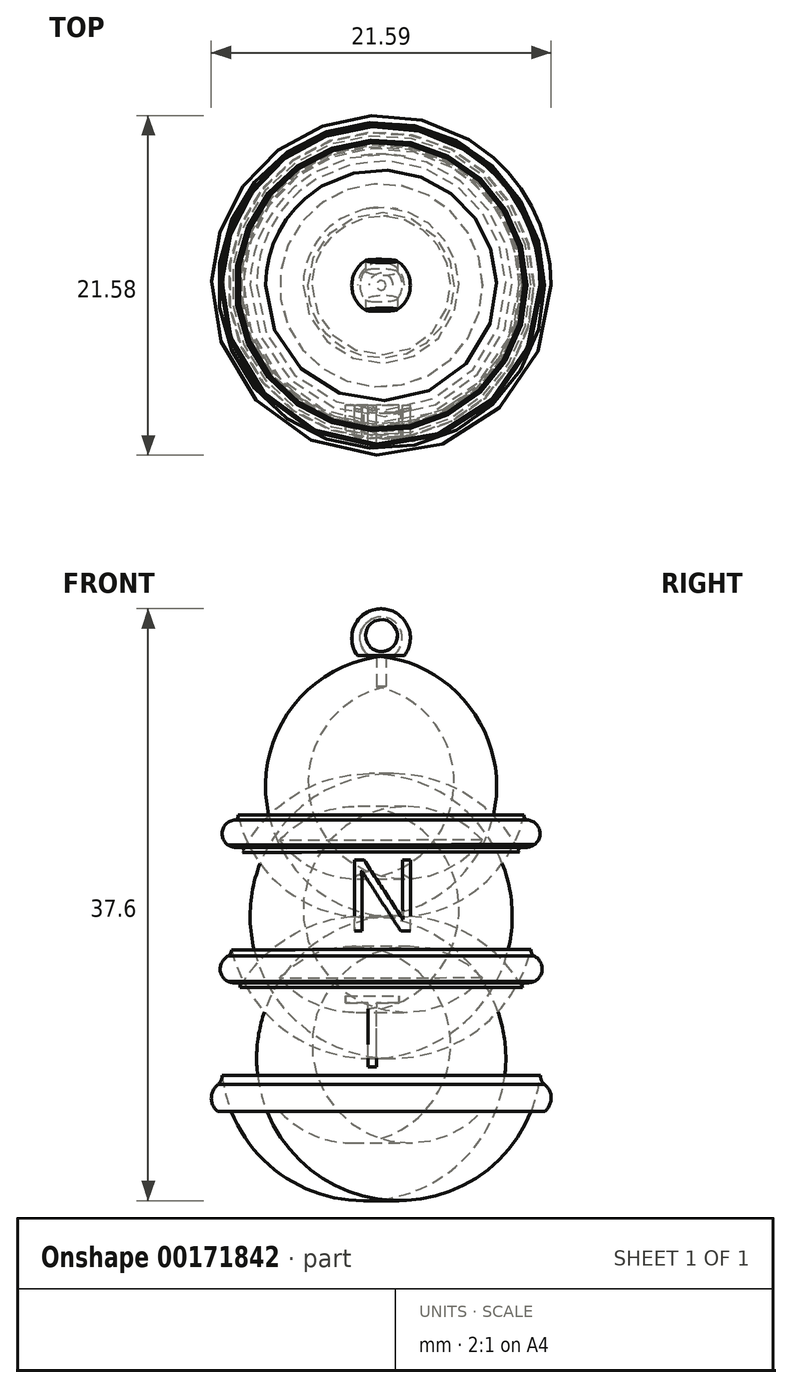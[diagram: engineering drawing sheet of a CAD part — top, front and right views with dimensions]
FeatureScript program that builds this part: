
annotation { "Feature Type Name" : "Feature", "Feature Type Description" : "" }
export const myFeature = defineFeature(function(context is Context, id is Id, definition is map)
    precondition{}
    {
        {
            var Q0;
            Q0=qCreatedBy(makeId("Front.planeOp"),FACE);
            var sketch = newSketch(context, id + "F0", { "sketchPlane" : qUnion([Q0])});
            skLineSegment(sketch, "E0.bottom", {"start": v(-21.86, 0.08) * mm, "end": v(-21.89, 0.08) * mm, "construction": true});
            skLineSegment(sketch, "E0.top", {"start": v(-9.19, 50.88) * mm, "end": v(-34.59, 50.88) * mm, "construction": true});
            skLineSegment(sketch, "E0.left", {"start": v(-9.19, 0.08) * mm, "end": v(-9.19, 50.88) * mm, "construction": true});
            skLineSegment(sketch, "E0.right", {"start": v(-34.59, 0.08) * mm, "end": v(-34.59, 50.88) * mm, "construction": true});
            skLineSegment(sketch, "E1.left", {"start": v(-34.48, 0.28) * mm, "end": v(-34.59, 0.08) * mm});
            skLineSegment(sketch, "E1.right", {"start": v(-44.55, 0.28) * mm, "end": v(-44.66, 0.08) * mm});
            skLineSegment(sketch, "E2", {"start": v(-31.55, 20.94) * mm, "end": v(-30.06, 20.94) * mm});
            skLineSegment(sketch, "E3", {"start": v(-21.86, -2.43) * mm, "end": v(-21.85, 22.57) * mm, "construction": true});
            skLineSegment(sketch, "E4", {"start": v(-31.55, 19.56) * mm, "end": v(-31.55, 14.27) * mm});
            skLineSegment(sketch, "E5", {"start": v(-31.44, 12.9) * mm, "end": v(-30.12, 12.9) * mm});
            skLineSegment(sketch, "E6", {"start": v(-29.62, 0.08) * mm, "end": v(-21.87, 0.08) * mm});
            skLineSegment(sketch, "E7", {"start": v(-30.06, 20.94) * mm, "end": v(-30.06, 14.45) * mm});
            skLineSegment(sketch, "E8", {"start": v(-30.06, 14.45) * mm, "end": v(-28.15, 14.45) * mm});
            skLineSegment(sketch, "E9", {"start": v(-30.12, 12.9) * mm, "end": v(-29.62, 0.08) * mm});
            skLineSegment(sketch, "E10", {"start": v(-28.15, 14.45) * mm, "end": v(-27.8, 1.73) * mm});
            skPoint(sketch, "E11.orphan", {"position": v(-26.25, 14.45) * mm});
            skLineSegment(sketch, "E12.trimOffspring", {"start": v(-29.62, 0.08) * mm, "end": v(-34.59, 0.08) * mm, "construction": true});
            skLineSegment(sketch, "E13", {"start": v(-27.8, 1.73) * mm, "end": v(-21.87, 1.73) * mm});
            skLineSegment(sketch, "E14", {"start": v(-21.87, 1.73) * mm, "end": v(-21.87, 0.08) * mm});
            skLineSegment(sketch, "E15.trimOffspring", {"start": v(-21.87, 0.08) * mm, "end": v(-29.62, 0.08) * mm, "construction": true});
            skArc(sketch, "E16", {"start": v(-31.55, 20.94) * mm, "mid": v(-32.24, 20.25) * mm, "end": v(-31.55, 19.56) * mm});
            skArc(sketch, "E17", {"start": v(-31.55, 14.27) * mm, "mid": v(-32.12, 13.53) * mm, "end": v(-31.44, 12.9) * mm});
            skSolve(sketch);
        }
        {
            var Q0;
            Q0=sQuery(id+"F0.wireOp",EDGE,"E2");
            var Q1;
            Q1=sQuery(id+"F0.wireOp",EDGE,"E7");
            var Q2;
            Q2=sQuery(id+"F0.wireOp",EDGE,"E16");
            var Q3;
            Q3=sQuery(id+"F0.wireOp",EDGE,"E4");
            var Q4;
            Q4=sQuery(id+"F0.wireOp",EDGE,"E17");
            var Q5;
            Q5=sQuery(id+"F0.wireOp",EDGE,"E5");
            var Q6;
            Q6=sQuery(id+"F0.wireOp",EDGE,"E8");
            var Q7;
            Q7=sQuery(id+"F0.wireOp",EDGE,"E10");
            var Q8;
            Q8=sQuery(id+"F0.wireOp",EDGE,"E9");
            var Q9;
            Q9=sQuery(id+"F0.wireOp",EDGE,"E6");
            var Q10;
            Q10=sQuery(id+"F0.wireOp",EDGE,"E13");
            var Q11;
            Q11=sQuery(id+"F0.wireOp",EDGE,"E3");
            revolve(context, id + "F1", {"bodyType" : ToolBodyType.SURFACE, "surfaceEntities" : qUnion([Q0, Q1, Q2, Q3, Q4, Q5, Q6, Q7, Q8, Q9, Q10]), "axis" : qUnion([Q11]), "revolveType" : RevolveType.FULL});
        }
        {
            var Q0;
            Q0=qCreatedBy(makeId("Front.planeOp"),FACE);
            var sketch = newSketch(context, id + "F2", { "sketchPlane" : qUnion([Q0])});
            skArc(sketch, "E18", {"start": v(-31, 28.57) * mm, "mid": v(-32.02, 25.86) * mm, "end": v(-32.14, 22.97) * mm});
            skArc(sketch, "E19", {"start": v(-30.83, 37.15) * mm, "mid": v(-31.74, 34.12) * mm, "end": v(-31.54, 30.96) * mm});
            skArc(sketch, "E20", {"start": v(-22.34, 49.62) * mm, "mid": v(-22.57, 49.64) * mm, "end": v(-22.8, 49.65) * mm});
            skPoint(sketch, "E21", {"position": v(-31.56, 20.72) * mm});
            skArc(sketch, "E22.trimOffspring", {"start": v(-22.31, 33.07) * mm, "mid": v(-22.53, 33.08) * mm, "end": v(-22.75, 33.1) * mm});
            skLineSegment(sketch, "E23", {"start": v(-22.05, 76.41) * mm, "end": v(-22.02, 13.63) * mm, "construction": true});
            skLineSegment(sketch, "E24", {"start": v(-22.34, 49.62) * mm, "end": v(-22.34, 47.66) * mm});
            skArc(sketch, "E25", {"start": v(-22.34, 47.66) * mm, "mid": v(-28.77, 44.9) * mm, "end": v(-28.48, 37.91) * mm});
            skArc(sketch, "E26", {"start": v(-28.48, 37.91) * mm, "mid": v(-30.16, 33.53) * mm, "end": v(-28.48, 29.15) * mm});
            skArc(sketch, "E27", {"start": v(-28.48, 29.15) * mm, "mid": v(-30.12, 24.93) * mm, "end": v(-28.48, 20.71) * mm});
            skArc(sketch, "E28", {"start": v(-32.4, 22.4) * mm, "mid": v(-32.82, 21.55) * mm, "end": v(-32.42, 20.7) * mm});
            skPoint(sketch, "E28.midSnap0", {"position": v(-32.16, 24.99) * mm});
            skArc(sketch, "E29", {"start": v(-31.72, 30.56) * mm, "mid": v(-32.25, 29.75) * mm, "end": v(-31.74, 28.93) * mm});
            skArc(sketch, "E30", {"start": v(-31.29, 39.2) * mm, "mid": v(-32.1, 38.58) * mm, "end": v(-31.78, 37.62) * mm});
            skArc(sketch, "E31", {"start": v(-31.74, 28.93) * mm, "mid": v(-31.44, 28.86) * mm, "end": v(-31.14, 28.85) * mm});
            skArc(sketch, "E32", {"start": v(-31.78, 37.62) * mm, "mid": v(-31.38, 37.47) * mm, "end": v(-30.96, 37.45) * mm});
            skLineSegment(sketch, "E33", {"start": v(-28.48, 20.71) * mm, "end": v(-32.42, 20.7) * mm});
            skArc(sketch, "E34", {"start": v(-31.29, 39.2) * mm, "mid": v(-31.14, 39.33) * mm, "end": v(-31.12, 39.53) * mm});
            skArc(sketch, "E35", {"start": v(-31.72, 30.56) * mm, "mid": v(-31.55, 30.87) * mm, "end": v(-31.6, 31.23) * mm});
            skArc(sketch, "E36", {"start": v(-31.02, 28.53) * mm, "mid": v(-31.02, 28.78) * mm, "end": v(-31.26, 28.85) * mm});
            skArc(sketch, "E37", {"start": v(-32.45, 22.34) * mm, "mid": v(-32.19, 22.7) * mm, "end": v(-32.16, 23.14) * mm});
            skPoint(sketch, "E38.orphan", {"position": v(-30.78, 28.93) * mm});
            skPoint(sketch, "E39", {"position": v(-22.05, 76.41) * mm});
            skArc(sketch, "E40", {"start": v(-30.83, 37.15) * mm, "mid": v(-30.78, 37.35) * mm, "end": v(-30.96, 37.45) * mm});
            skArc(sketch, "E41", {"start": v(-22.04, 52.62) * mm, "mid": v(-23.7, 51.58) * mm, "end": v(-23.52, 49.63) * mm});
            skArc(sketch, "E42", {"start": v(-22.04, 52.1) * mm, "mid": v(-23.32, 51.16) * mm, "end": v(-22.8, 49.65) * mm});
            skArc(sketch, "E43.trimOffspring", {"start": v(-23.52, 49.63) * mm, "mid": v(-29.66, 46.33) * mm, "end": v(-31.12, 39.51) * mm});
            skLineSegment(sketch, "E44", {"start": v(-22.04, 52.62) * mm, "end": v(-22.04, 52.1) * mm});
            skSolve(sketch);
        }
        {
            var Q0;
            Q0 = qSketchRegion(id + "F2", true);
            var Q1;
            Q1=sQuery(id+"F2.wireOp",EDGE,"E23");
            revolve(context, id + "F3", {"entities" : qUnion([Q0]), "axis" : qUnion([Q1]), "revolveType" : RevolveType.FULL});
        }
        {
            var Q0;
            Q0=qCreatedBy(makeId("Front.planeOp"),FACE);
            cPlane(context, id + "F4", {"entities" : qUnion([Q0]), "cplaneType" : CPlaneType.OFFSET, "offset" : 7.62 * mm, "width" : 152.4 * mm, "height" : 152.4 * mm});
        }
        {
            var Q0;
            Q0=qCreatedBy(id+"F4.planeOp",FACE);
            var sketch = newSketch(context, id + "F5", { "sketchPlane" : qUnion([Q0])});
            skText(sketch, "E45", { "text": "C\nN\nT", "fontName": "OpenSans-Regular.ttf"});
            const initialGuessF5  = {"E45": [-0.02434, 0.04077, 1, 0, 0.00457]};
            skSetInitialGuess(sketch, initialGuessF5);
            skSolve(sketch);
        }
        {
            var Q0;
            Q0 = qSketchRegion(id + "F5", true);
            extrude(context, id + "F6", {"entities" : qUnion([Q0]), "operationType" : NewBodyOperationType.REMOVE, "depth" : 3.8 * mm});
        }
        {
            var Q0;
            Q0=qCreatedBy(id+"F4.planeOp",FACE);
            var sketch = newSketch(context, id + "F7", { "sketchPlane" : qUnion([Q0])});
            skCircle(sketch, "E46", {"center": v(-22, 50.91) * mm, "radius": 1.01 * mm});
            skSolve(sketch);
        }
        {
            var Q0;
            Q0 = qSketchRegion(id + "F7", true);
            extrude(context, id + "F8", {"entities" : qUnion([Q0]), "operationType" : NewBodyOperationType.REMOVE, "oppositeDirection" : true, "depth" : 25.4 * mm});
        }
    });
